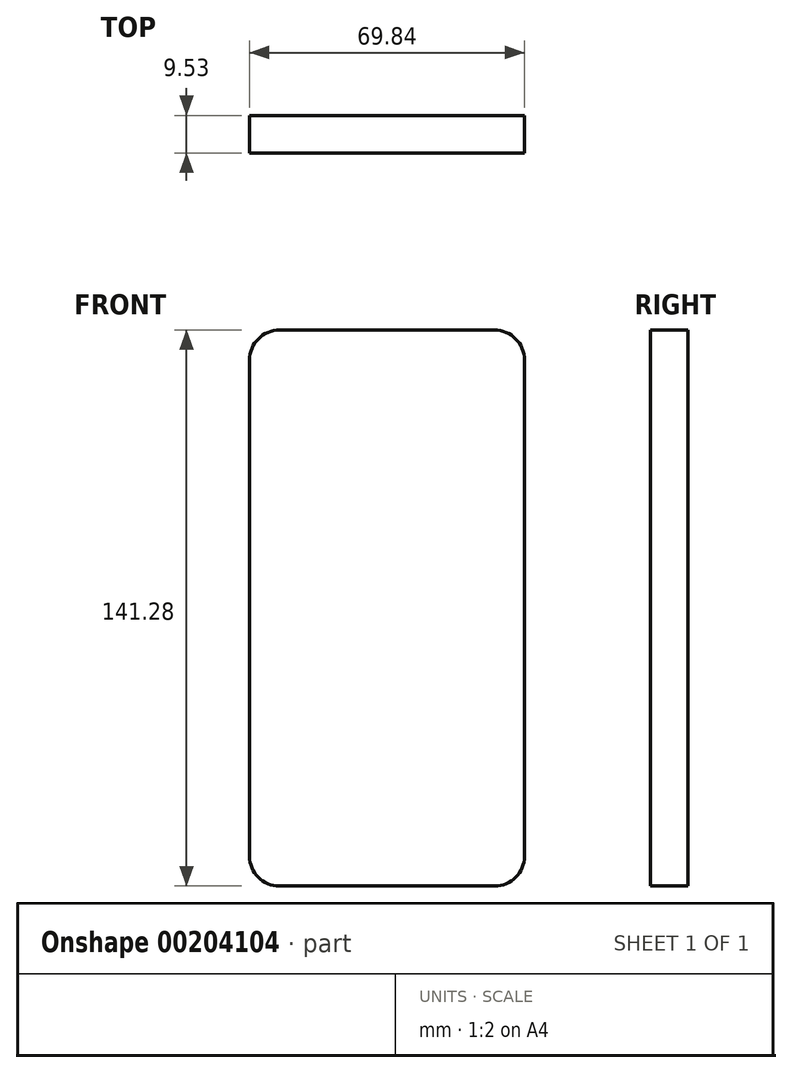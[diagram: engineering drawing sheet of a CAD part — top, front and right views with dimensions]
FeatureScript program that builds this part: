
annotation { "Feature Type Name" : "Feature", "Feature Type Description" : "" }
export const myFeature = defineFeature(function(context is Context, id is Id, definition is map)
    precondition{}
    {
        {
            var Q0;
            Q0=qCreatedBy(makeId("Front.planeOp"),FACE);
            var sketch = newSketch(context, id + "F0", { "sketchPlane" : qUnion([Q0])});
            skLineSegment(sketch, "E0.bottom", {"start": v(-34.93, 70.64) * mm, "end": v(34.93, 70.64) * mm});
            skLineSegment(sketch, "E0.top", {"start": v(-34.93, -70.64) * mm, "end": v(34.93, -70.64) * mm});
            skLineSegment(sketch, "E0.left", {"start": v(-34.92, 70.64) * mm, "end": v(-34.93, -70.64) * mm});
            skLineSegment(sketch, "E0.right", {"start": v(34.93, 70.64) * mm, "end": v(34.92, -70.64) * mm});
            skLineSegment(sketch, "E1", {"start": v(0, 70.64) * mm, "end": v(0, -70.64) * mm, "construction": true});
            skLineSegment(sketch, "E2", {"start": v(34.92, 0) * mm, "end": v(-34.92, 0) * mm, "construction": true});
            skSolve(sketch);
        }
        {
            var Q0;
            Q0 = qSketchRegion(id + "F0", true);
            extrude(context, id + "F1", {"entities" : qUnion([Q0]), "depth" : 9.52 * mm});
        }
        {
            var Q0;
            Q0=makeQuery(id+"F1.opExtrude","SWEPT_EDGE",EDGE,{"disambiguationData":[OSD([sQuery(id+"F0.wireOp",EDGE,"E0.bottom"),sQuery(id+"F0.wireOp",EDGE,"E0.right")])]});
            var Q1;
            Q1=makeQuery(id+"F1.opExtrude","SWEPT_EDGE",EDGE,{"disambiguationData":[OSD([sQuery(id+"F0.wireOp",EDGE,"E0.bottom"),sQuery(id+"F0.wireOp",EDGE,"E0.left")])]});
            var Q2;
            Q2=makeQuery(id+"F1.opExtrude","SWEPT_EDGE",EDGE,{"disambiguationData":[OSD([sQuery(id+"F0.wireOp",EDGE,"E0.top"),sQuery(id+"F0.wireOp",EDGE,"E0.left")])]});
            var Q3;
            Q3=makeQuery(id+"F1.opExtrude","SWEPT_EDGE",EDGE,{"disambiguationData":[OSD([sQuery(id+"F0.wireOp",EDGE,"E0.top"),sQuery(id+"F0.wireOp",EDGE,"E0.right")])]});
            fillet(context, id + "F2", {"entities" : qUnion([Q0, Q1, Q2, Q3]), "radius" : 7.62 * mm, "tangentPropagation" : true, "allowEdgeOverflow" : false});
        }
    });
